# Revit family: GRIPPLE FAST TRAK M3_2TIER
name_source: partatom
category: Generic Models
revit_build: Autodesk Revit 2017 (Build: 20190508_0315(x64)
units: mm (PartAtom-declared; Revit-internal decimal feet)

## family parameters
Always vertical = Yes
Can host rebar = No
Cut with Voids When Loaded = No
Part Type = Normal
Room Calculation Point = No
Round Connector Dimension = Use Diameter
Shared = No
Work Plane-Based = Yes

## types (14) — shared parameters
Default Elevation = 1219 mm
Manufacturer = Gripple Ltd
URL = https://www.gripple.com

## per-type parameters (varying)
| type | FTB | FTT SPLIT |
| FTB-170 | FTB : FTB-170 | 96 mm |
| FTB-270 | FTB : FTB-270 | 146 mm |
| FTB-370 | FTB : FTB-370 | 196 mm |
| FTB-470 | FTB : FTB-470 | 246 mm |
| FTB-570 | FTB : FTB-570 | 296 mm |
| FTB-670 | FTB : FTB-670 | 346 mm |
| FTB-770 | FTB : FTB-770 | 396 mm |
| FTB-870 | FTB : FTB-870 | 446 mm |
| FTB-970 | FTB : FTB-970 | 496 mm |
| FTB-1070 | FTB : FTB-1070 | 546 mm |
| FTB-1170 | FTB : FTB-1170 | 596 mm |
| FTB-1270 | FTB : FTB-1270 | 646 mm |
| FTB-1370 | FTB : FTB-1370 | 696 mm |
| FTB-1470 | FTB : FTB-1470 | 746 mm |

## geometry (parser evidence)
native form markers: Sweep x17
no freeform markers — native parametric forms only
